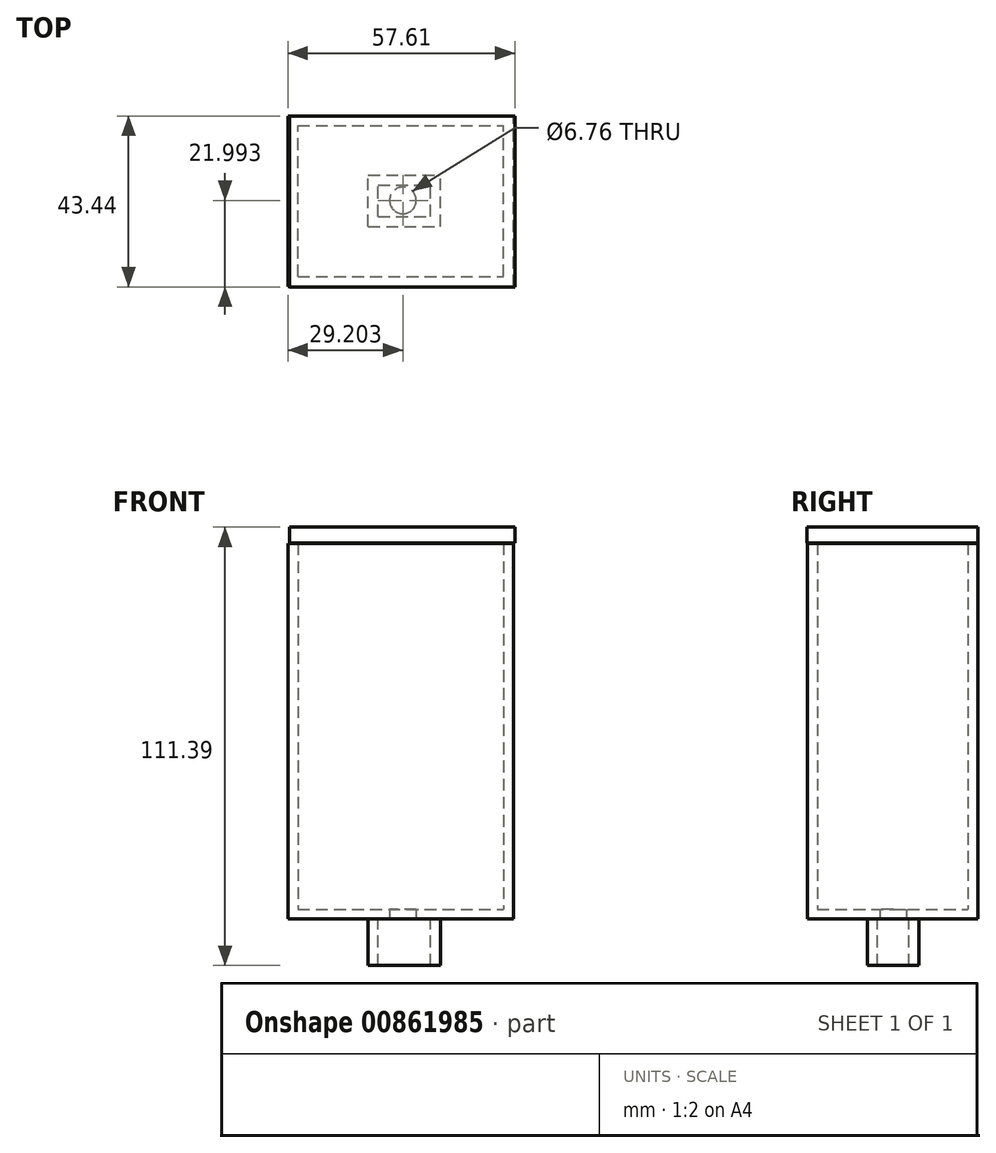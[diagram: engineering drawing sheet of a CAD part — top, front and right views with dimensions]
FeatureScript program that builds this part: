
annotation { "Feature Type Name" : "Feature", "Feature Type Description" : "" }
export const myFeature = defineFeature(function(context is Context, id is Id, definition is map)
    precondition{}
    {
        {
            var Q0;
            Q0=qCreatedBy(makeId("Front.planeOp"),FACE);
            var sketch = newSketch(context, id + "F0", { "sketchPlane" : qUnion([Q0])});
            skLineSegment(sketch, "E0.bottom", {"start": v(-27.36, 44.07) * mm, "end": v(29.87, 44.07) * mm});
            skLineSegment(sketch, "E0.top", {"start": v(-27.36, -51.4) * mm, "end": v(29.87, -51.4) * mm});
            skLineSegment(sketch, "E0.left", {"start": v(-27.36, 44.07) * mm, "end": v(-27.36, -51.4) * mm});
            skLineSegment(sketch, "E0.right", {"start": v(29.87, 44.07) * mm, "end": v(29.87, -51.4) * mm});
            skSolve(sketch);
        }
        {
            var Q0;
            Q0=makeQuery(id+"F0.imprint","IMPRINT",FACE,{"disambiguationData":[TD([[makeQuery(id+"F0.imprint","IMPRINT",EDGE,{"derivedFrom":sQuery(id+"F0.wireOp",EDGE,"E0.bottom")}),-1.0]])]});
            extrude(context, id + "F1", {"entities" : qUnion([Q0]), "depth" : 43.3 * mm, "offsetDistance" : 25 * mm});
        }
        {
            var Q0;
            Q0=makeQuery(id+"F1.opExtrude","SWEPT_FACE",FACE,{"disambiguationData":[OSD([sQuery(id+"F0.wireOp",EDGE,"E0.bottom")])]});
            shell(context, id + "F2", {"entities" : qUnion([Q0]), "thickness" : 2.5 * mm});
        }
        {
            var Q0;
            Q0=makeQuery(id+"F1.opExtrude","SWEPT_FACE",FACE,{"disambiguationData":[OSD([sQuery(id+"F0.wireOp",EDGE,"E0.top")])]});
            var sketch = newSketch(context, id + "F3", { "sketchPlane" : qUnion([Q0])});
            skLineSegment(sketch, "E1.bottom", {"start": v(-6.98, 28.04) * mm, "end": v(11.33, 28.04) * mm});
            skLineSegment(sketch, "E1.top", {"start": v(-6.98, 15) * mm, "end": v(11.33, 15) * mm});
            skLineSegment(sketch, "E1.left", {"start": v(-6.98, 28.04) * mm, "end": v(-6.98, 15) * mm});
            skLineSegment(sketch, "E1.right", {"start": v(11.33, 28.04) * mm, "end": v(11.33, 15) * mm});
            skSolve(sketch);
        }
        {
            var Q0;
            Q0=makeQuery(id+"F3.imprint","IMPRINT",FACE,{"disambiguationData":[TD([[makeQuery(id+"F3.imprint","IMPRINT",EDGE,{"derivedFrom":sQuery(id+"F3.wireOp",EDGE,"E1.bottom")}),-1.0]])]});
            extrude(context, id + "F4", {"entities" : qUnion([Q0]), "operationType" : NewBodyOperationType.ADD, "depth" : 11.8 * mm, "offsetDistance" : 25 * mm});
        }
        {
            var Q0;
            Q0=makeQuery(id+"F4.opExtrude","CAP_FACE",FACE,{"disambiguationData":[OSD([sQuery(id+"F3.wireOp",EDGE,"E1.bottom"),sQuery(id+"F3.wireOp",EDGE,"E1.top"),sQuery(id+"F3.wireOp",EDGE,"E1.left"),sQuery(id+"F3.wireOp",EDGE,"E1.right")])],"isStart":false});
            shell(context, id + "F5", {"entities" : qUnion([Q0]), "thickness" : 2.5 * mm});
        }
        {
            var Q0;
            Q0=makeQuery(id+"F5.opShell","OFFSET_FACE",FACE,{"disambiguationData":[OSD([sQuery(id+"F0.wireOp",EDGE,"E0.top")])]});
            var sketch = newSketch(context, id + "F6", { "sketchPlane" : qUnion([Q0])});
            skCircle(sketch, "E2.cCircle", {"center": v(1.84, 21.45) * mm, "radius": 3.2 * mm, "construction": true});
            skLineSegment(sketch, "E2.0", {"start": v(-1.36, 20.4) * mm, "end": v(-1.36, 22.49) * mm});
            skLineSegment(sketch, "E2.1", {"start": v(-1.36, 22.49) * mm, "end": v(-0.14, 24.17) * mm});
            skLineSegment(sketch, "E2.2", {"start": v(-0.14, 24.17) * mm, "end": v(1.84, 24.81) * mm});
            skLineSegment(sketch, "E2.3", {"start": v(1.84, 24.81) * mm, "end": v(3.82, 24.17) * mm});
            skLineSegment(sketch, "E2.4", {"start": v(3.82, 24.17) * mm, "end": v(5.04, 22.49) * mm});
            skLineSegment(sketch, "E2.5", {"start": v(5.04, 22.49) * mm, "end": v(5.04, 20.4) * mm});
            skLineSegment(sketch, "E2.6", {"start": v(5.04, 20.4) * mm, "end": v(3.82, 18.72) * mm});
            skLineSegment(sketch, "E2.7", {"start": v(3.82, 18.72) * mm, "end": v(1.84, 18.08) * mm});
            skLineSegment(sketch, "E2.8", {"start": v(1.84, 18.08) * mm, "end": v(-0.14, 18.72) * mm});
            skLineSegment(sketch, "E2.9", {"start": v(-0.14, 18.72) * mm, "end": v(-1.36, 20.4) * mm});
            skPoint(sketch, "E2.0.midPoint", {"position": v(-1.36, 21.45) * mm});
            skSolve(sketch);
        }
        {
            var Q0;
            Q0=sQuery(id+"F6.wireOp",VERTEX,"E2.cCircle.center");
            var Q1;
            Q1=makeQuery(id+"F1.opExtrude","SWEPT_BODY",BODY,{"disambiguationData":[OSD([sQuery(id+"F0.wireOp",EDGE,"E0.bottom"),sQuery(id+"F0.wireOp",EDGE,"E0.top"),sQuery(id+"F0.wireOp",EDGE,"E0.left"),sQuery(id+"F0.wireOp",EDGE,"E0.right")])]});
            hole(context, id + "F7", {"style" : HoleStyle.SIMPLE, "endStyle" : HoleEndStyle.THROUGH, "standardTappedOrClearance" : lookupTablePath({ "fit" : "Normal (ASME)", "standard" : "ANSI", "size" : "1/4", "type" : "Clearance" }), "standardBlindInLast" : lookupTablePath({ "fit" : "Free", "standard" : "ANSI", "size" : "1/4", "type" : "Clearance" }), "holeDiameter" : 6.76 * mm, "majorDiameter" : 5 * mm, "isTappedThrough" : true, "tappedDepth" : 12 * mm, "tapClearance" : 3, "locations" : qUnion([Q0]), "scope" : qUnion([Q1])});
        }
        {
            var Q0;
            Q0=qCreatedBy(makeId("Top.planeOp"),FACE);
            cPlane(context, id + "F8", {"entities" : qUnion([Q0]), "cplaneType" : CPlaneType.OFFSET, "offset" : 44.2 * mm, "width" : 150 * mm, "height" : 150 * mm});
        }
        {
            var Q0;
            Q0=qCreatedBy(id+"F8.planeOp",FACE);
            var sketch = newSketch(context, id + "F9", { "sketchPlane" : qUnion([Q0])});
            skLineSegment(sketch, "E3.bottom", {"start": v(-27.04, 0) * mm, "end": v(-26.99, 0) * mm});
            skLineSegment(sketch, "E3.top", {"start": v(-27.04, -43.44) * mm, "end": v(-26.99, -43.44) * mm});
            skLineSegment(sketch, "E3.left", {"start": v(-27.04, 0) * mm, "end": v(-27.04, -43.44) * mm});
            skLineSegment(sketch, "E3.right", {"start": v(-26.99, 0) * mm, "end": v(-26.99, -43.44) * mm});
            skLineSegment(sketch, "E4.bottom", {"start": v(30.25, -43.44) * mm, "end": v(-26.99, -43.44) * mm});
            skLineSegment(sketch, "E4.top", {"start": v(30.25, 0) * mm, "end": v(-26.99, 0) * mm});
            skLineSegment(sketch, "E4.left", {"start": v(30.25, -43.44) * mm, "end": v(30.25, 0) * mm});
            skLineSegment(sketch, "E4.right", {"start": v(-26.99, -43.44) * mm, "end": v(-26.99, 0) * mm});
            skSolve(sketch);
        }
        {
            var Q0;
            Q0=makeQuery(id+"F9.imprint","IMPRINT",FACE,{"disambiguationData":[TD([[makeQuery(id+"F9.imprint","IMPRINT",EDGE,{"derivedFrom":sQuery(id+"F9.wireOp",EDGE,"E4.bottom")}),-1.0]])]});
            extrude(context, id + "F10", {"entities" : qUnion([Q0]), "depth" : 4 * mm, "offsetDistance" : 25 * mm});
        }
    });
